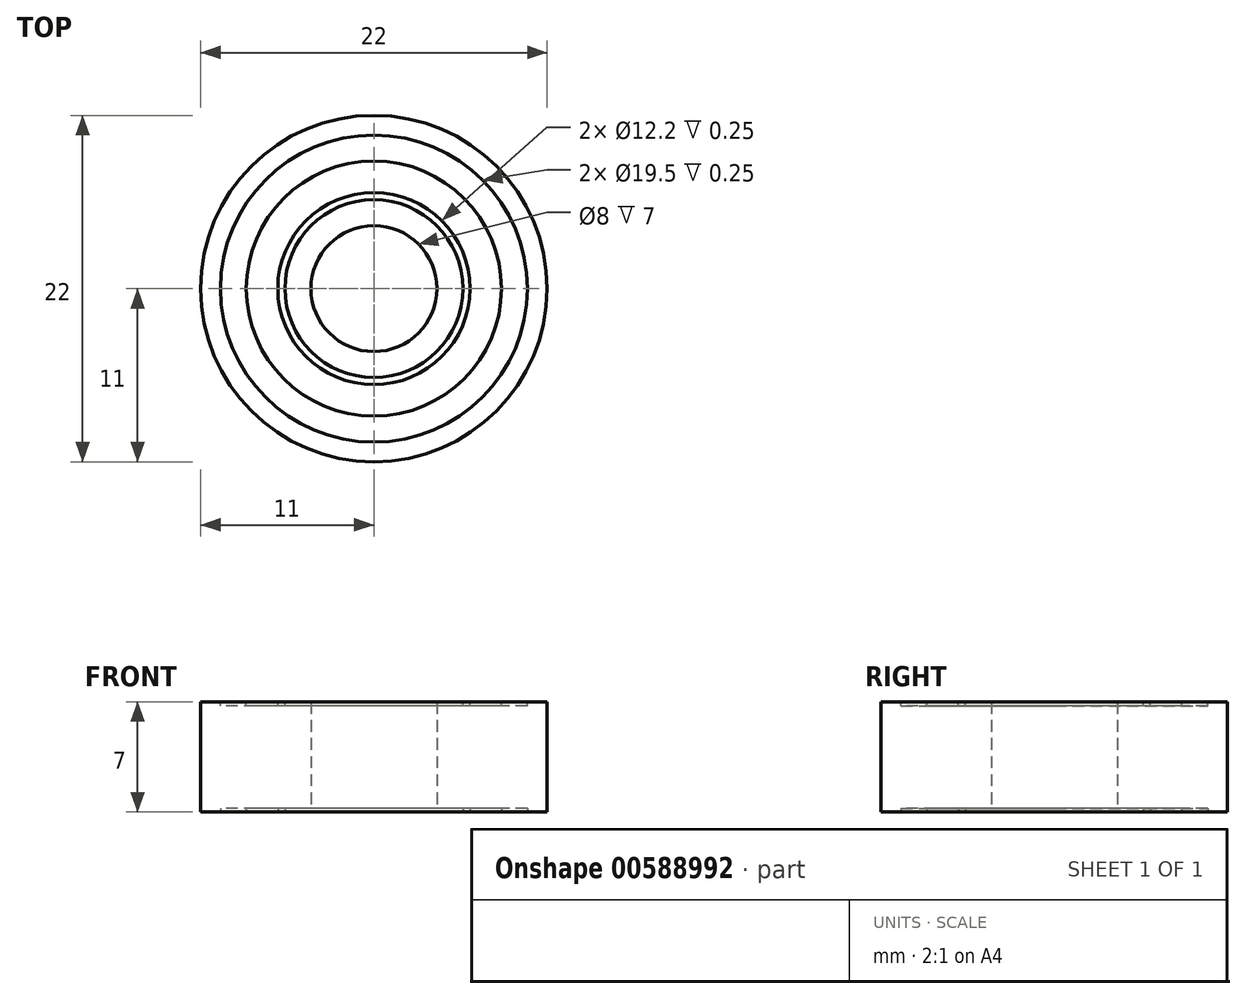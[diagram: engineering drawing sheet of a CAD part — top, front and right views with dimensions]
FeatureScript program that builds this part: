
annotation { "Feature Type Name" : "Feature", "Feature Type Description" : "" }
export const myFeature = defineFeature(function(context is Context, id is Id, definition is map)
    precondition{}
    {
        {
            var Q0;
            Q0=qCreatedBy(makeId("Top.planeOp"),FACE);
            var sketch = newSketch(context, id + "F0", { "sketchPlane" : qUnion([Q0])});
            skCircle(sketch, "E0", {"center": v(0, 0) * mm, "radius": 4 * mm});
            skCircle(sketch, "E1", {"center": v(0, 0) * mm, "radius": 5.65 * mm});
            skCircle(sketch, "E2", {"center": v(0, 0) * mm, "radius": 11 * mm});
            skCircle(sketch, "E3", {"center": v(0, 0) * mm, "radius": 6.1 * mm});
            skCircle(sketch, "E4", {"center": v(0, 0) * mm, "radius": 8.1 * mm});
            skCircle(sketch, "E5", {"center": v(0, 0) * mm, "radius": 9.75 * mm});
            skSolve(sketch);
        }
        {
            var Q0;
            Q0 = qSketchRegion(id + "F0", true);
            var Q1;
            Q1=makeQuery(id+"F0.imprint","IMPRINT",FACE,{"disambiguationData":[TD([[makeQuery(id+"F0.imprint","IMPRINT",EDGE,{"derivedFrom":sQuery(id+"F0.wireOp",EDGE,"E0")}),-1.0]])]});
            var Q2;
            Q2=makeQuery(id+"F0.imprint","IMPRINT",FACE,{"disambiguationData":[TD([[makeQuery(id+"F0.imprint","IMPRINT",EDGE,{"derivedFrom":sQuery(id+"F0.wireOp",EDGE,"E1")}),-1.0]])]});
            var Q3;
            Q3=makeQuery(id+"F0.imprint","IMPRINT",FACE,{"disambiguationData":[TD([[makeQuery(id+"F0.imprint","IMPRINT",EDGE,{"derivedFrom":sQuery(id+"F0.wireOp",EDGE,"E3")}),-1.0]])]});
            var Q4;
            Q4=makeQuery(id+"F0.imprint","IMPRINT",FACE,{"disambiguationData":[TD([[makeQuery(id+"F0.imprint","IMPRINT",EDGE,{"derivedFrom":sQuery(id+"F0.wireOp",EDGE,"E4")}),-1.0]])]});
            var Q5;
            Q5=makeQuery(id+"F0.imprint","IMPRINT",FACE,{"disambiguationData":[TD([[makeQuery(id+"F0.imprint","IMPRINT",EDGE,{"derivedFrom":sQuery(id+"F0.wireOp",EDGE,"E3")}),1.0]])]});
            extrude(context, id + "F1", {"entities" : qUnion([Q0, Q1, Q2, Q3, Q4, Q5]), "depth" : (7 / 2) * mm, "offsetDistance" : 25 * mm});
        }
        {
            var Q0;
            Q0=makeQuery(id+"F0.imprint","IMPRINT",FACE,{"disambiguationData":[TD([[makeQuery(id+"F0.imprint","IMPRINT",EDGE,{"derivedFrom":sQuery(id+"F0.wireOp",EDGE,"E1")}),-1.0]])]});
            var Q1;
            Q1=makeQuery(id+"F0.imprint","IMPRINT",FACE,{"disambiguationData":[TD([[makeQuery(id+"F0.imprint","IMPRINT",EDGE,{"derivedFrom":sQuery(id+"F0.wireOp",EDGE,"E4")}),-1.0]])]});
            extrude(context, id + "F2", {"entities" : qUnion([Q0, Q1]), "operationType" : NewBodyOperationType.REMOVE, "depth" : 0.25 * mm, "offsetDistance" : 25 * mm});
        }
        {
            var Q0;
            Q0=makeQuery(id+"F1.opExtrude","SWEPT_BODY",BODY,{"disambiguationData":[OSD([sQuery(id+"F0.wireOp",EDGE,"E0"),sQuery(id+"F0.wireOp",EDGE,"E2")])]});
            var Q1;
            Q1=makeQuery(id+"F1.opExtrude","CAP_FACE",FACE,{"disambiguationData":[OSD([sQuery(id+"F0.wireOp",EDGE,"E0"),sQuery(id+"F0.wireOp",EDGE,"E2")])],"isStart":false});
            mirror(context, id + "F3", {"operationType" : NewBodyOperationType.ADD, "entities" : qUnion([Q0]), "mirrorPlane" : qUnion([Q1])});
        }
    });
